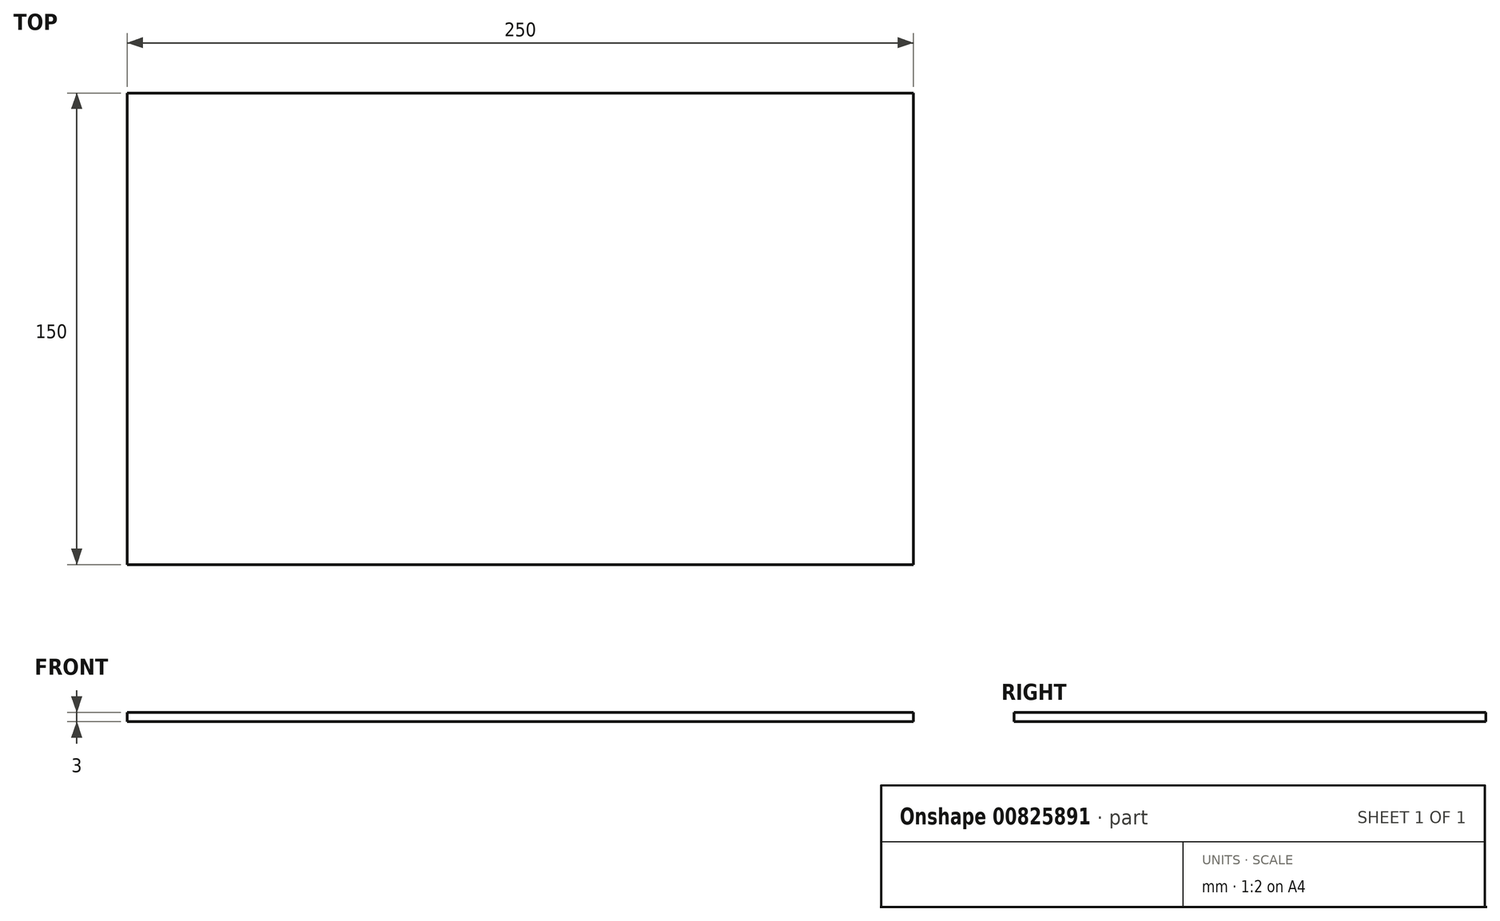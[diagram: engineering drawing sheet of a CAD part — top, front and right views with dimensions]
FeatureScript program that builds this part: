
annotation { "Feature Type Name" : "Feature", "Feature Type Description" : "" }
export const myFeature = defineFeature(function(context is Context, id is Id, definition is map)
    precondition{}
    {
        {
            var Q0;
            Q0=qCreatedBy(makeId("Top.planeOp"),FACE);
            var sketch = newSketch(context, id + "F0", { "sketchPlane" : qUnion([Q0])});
            skLineSegment(sketch, "E0.bottom", {"start": v(125, -75) * mm, "end": v(-125, -75) * mm});
            skLineSegment(sketch, "E0.top", {"start": v(125, 75) * mm, "end": v(-125, 75) * mm});
            skLineSegment(sketch, "E0.left", {"start": v(125, -75) * mm, "end": v(125, 75) * mm});
            skLineSegment(sketch, "E0.right", {"start": v(-125, -75) * mm, "end": v(-125, 75) * mm});
            skPoint(sketch, "E0.middle", {"position": v(0, 0) * mm});
            skSolve(sketch);
        }
        {
            var Q0;
            Q0=makeQuery(id+"F0.imprint","IMPRINT",FACE,{"disambiguationData":[TD([[makeQuery(id+"F0.imprint","IMPRINT",EDGE,{"derivedFrom":sQuery(id+"F0.wireOp",EDGE,"E0.bottom")}),-1.0]])]});
            extrude(context, id + "F1", {"entities" : qUnion([Q0]), "endBound" : BoundingType.SYMMETRIC, "depth" : 3 * mm, "offsetDistance" : 25.4 * mm});
        }
    });
